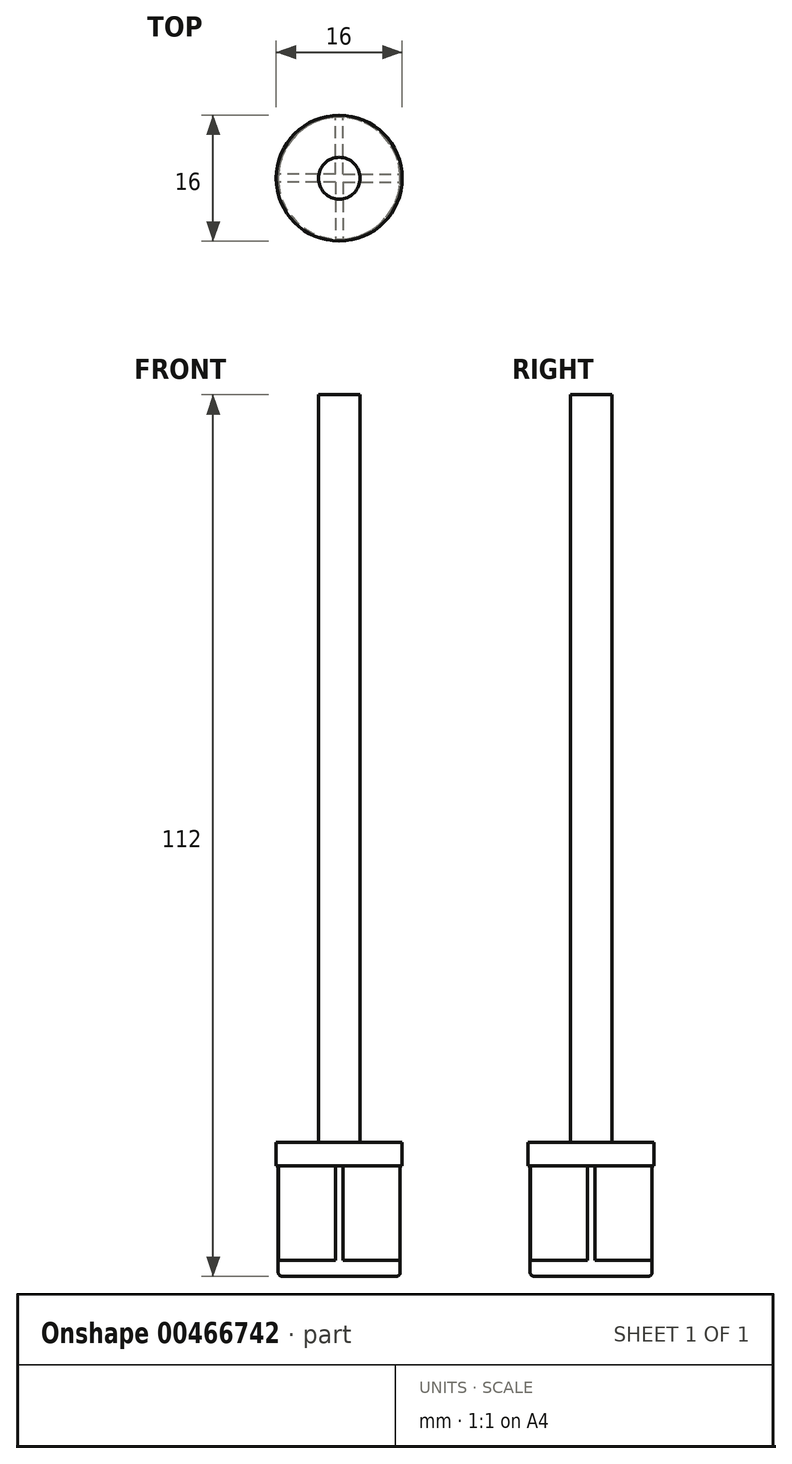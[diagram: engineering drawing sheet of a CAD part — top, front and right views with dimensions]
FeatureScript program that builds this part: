
annotation { "Feature Type Name" : "Feature", "Feature Type Description" : "" }
export const myFeature = defineFeature(function(context is Context, id is Id, definition is map)
    precondition{}
    {
        {
            var Q0;
            Q0=qCreatedBy(makeId("Top.planeOp"),FACE);
            var sketch = newSketch(context, id + "F0", { "sketchPlane" : qUnion([Q0])});
            skCircle(sketch, "E0", {"center": v(0, 0) * mm, "radius": 7.75 * mm});
            skSolve(sketch);
        }
        {
            var Q0;
            Q0=makeQuery(id+"F0.imprint","IMPRINT",FACE,{"disambiguationData":[TD([[makeQuery(id+"F0.imprint","IMPRINT",EDGE,{"derivedFrom":sQuery(id+"F0.wireOp",EDGE,"E0")}),1.0]])]});
            extrude(context, id + "F1", {"entities" : qUnion([Q0]), "depth" : 2 * mm, "offsetDistance" : 25 * mm});
        }
        {
            var Q0;
            Q0=makeQuery(id+"F1.opExtrude","CAP_FACE",FACE,{"disambiguationData":[OSD([sQuery(id+"F0.wireOp",EDGE,"E0")])],"isStart":false});
            var sketch = newSketch(context, id + "F2", { "sketchPlane" : qUnion([Q0])});
            skPoint(sketch, "E1", {"position": v(0, 3.88) * mm});
            skPoint(sketch, "E2", {"position": v(-3.88, 0) * mm});
            skPoint(sketch, "E3", {"position": v(0, -3.88) * mm});
            skPoint(sketch, "E4", {"position": v(3.88, 0) * mm});
            skLineSegment(sketch, "E5.top", {"start": v(0.5, 7.75) * mm, "end": v(-0.5, 7.75) * mm});
            skLineSegment(sketch, "E5.left", {"start": v(0.5, 0) * mm, "end": v(0.5, 7.75) * mm});
            skLineSegment(sketch, "E5.right", {"start": v(-0.5, 0) * mm, "end": v(-0.5, 7.75) * mm});
            skLineSegment(sketch, "E6.bottom", {"start": v(0, -0.5) * mm, "end": v(-7.75, -0.5) * mm});
            skLineSegment(sketch, "E6.top", {"start": v(0, 0.5) * mm, "end": v(-7.75, 0.5) * mm});
            skLineSegment(sketch, "E6.right", {"start": v(-7.75, -0.5) * mm, "end": v(-7.75, 0.5) * mm});
            skLineSegment(sketch, "E7.bottom", {"start": v(0, 0.5) * mm, "end": v(7.75, 0.5) * mm});
            skLineSegment(sketch, "E7.top", {"start": v(0, -0.5) * mm, "end": v(7.75, -0.5) * mm});
            skLineSegment(sketch, "E7.right", {"start": v(7.75, 0.5) * mm, "end": v(7.75, -0.5) * mm});
            skLineSegment(sketch, "E8.top", {"start": v(0.5, -7.75) * mm, "end": v(-0.5, -7.75) * mm});
            skLineSegment(sketch, "E8.left", {"start": v(0.5, 0) * mm, "end": v(0.5, -7.75) * mm});
            skLineSegment(sketch, "E8.right", {"start": v(-0.5, 0) * mm, "end": v(-0.5, -7.75) * mm});
            skSolve(sketch);
        }
        {
            var Q0;
            {var subQ10=sQuery(id+"F2.wireOp",EDGE,"E8.left");var subQ13=sQuery(id+"F2.wireOp",EDGE,"E5.left");var subQ15=makeQuery(id+"F2.imprint","INTERSECT",VERTEX,{"derivedFrom":[subQ13,subQ10]});Q0=makeQuery(id+"F2.imprint","IMPRINT",FACE,{"disambiguationData":[TD([[makeQuery(id+"F2.imprint","IMPRINT",EDGE,{"disambiguationData":[TD([[subQ15,-1.0]])],"derivedFrom":subQ13}),1.0]])]});}
            var Q1;
            {var subQ1=sQuery(id+"F2.wireOp",EDGE,"E5.right");var subQ5=sQuery(id+"F2.wireOp",EDGE,"E8.right");var subQ6=makeQuery(id+"F2.imprint","INTERSECT",VERTEX,{"derivedFrom":[subQ1,subQ5]});Q1=makeQuery(id+"F2.imprint","IMPRINT",FACE,{"disambiguationData":[TD([[makeQuery(id+"F2.imprint","IMPRINT",EDGE,{"disambiguationData":[TD([[subQ6,-1.0]])],"derivedFrom":subQ1}),1.0]])]});}
            var Q2;
            {var subQ0=sQuery(id+"F2.wireOp",EDGE,"E7.bottom");var subQ3=sQuery(id+"F2.wireOp",EDGE,"E5.left");var subQ4=makeQuery(id+"F2.imprint","INTERSECT",VERTEX,{"derivedFrom":[subQ3,subQ0]});Q2=makeQuery(id+"F2.imprint","IMPRINT",FACE,{"disambiguationData":[TD([[makeQuery(id+"F2.imprint","IMPRINT",EDGE,{"disambiguationData":[TD([[subQ4,-1.0]])],"derivedFrom":subQ3}),1.0]])]});}
            var Q3;
            {var subQ0=sQuery(id+"F2.wireOp",EDGE,"E8.left");var subQ1=sQuery(id+"F2.wireOp",EDGE,"E5.left");var subQ2=makeQuery(id+"F2.imprint","INTERSECT",VERTEX,{"derivedFrom":[subQ1,subQ0]});Q3=makeQuery(id+"F2.imprint","IMPRINT",FACE,{"disambiguationData":[TD([[makeQuery(id+"F2.imprint","IMPRINT",EDGE,{"disambiguationData":[TD([[subQ2,-1.0]])],"derivedFrom":subQ1}),-1.0]])]});}
            var Q4;
            {var subQ1=sQuery(id+"F2.wireOp",EDGE,"E6.bottom");var subQ5=sQuery(id+"F2.wireOp",EDGE,"E7.top");var subQ6=makeQuery(id+"F2.imprint","INTERSECT",VERTEX,{"derivedFrom":[subQ1,subQ5]});Q4=makeQuery(id+"F2.imprint","IMPRINT",FACE,{"disambiguationData":[TD([[makeQuery(id+"F2.imprint","IMPRINT",EDGE,{"disambiguationData":[TD([[subQ6,-1.0]])],"derivedFrom":subQ1}),1.0]])]});}
            extrude(context, id + "F3", {"entities" : qUnion([Q0, Q1, Q2, Q3, Q4]), "operationType" : NewBodyOperationType.ADD, "depth" : 12 * mm, "offsetDistance" : 25 * mm});
        }
        {
            var Q0;
            Q0=makeQuery(id+"F3.opExtrude","CAP_FACE",FACE,{"disambiguationData":[OSD([sQuery(id+"F0.wireOp",EDGE,"E0"),sQuery(id+"F2.wireOp",EDGE,"E5.left"),sQuery(id+"F2.wireOp",EDGE,"E5.right"),sQuery(id+"F2.wireOp",EDGE,"E6.bottom"),sQuery(id+"F2.wireOp",EDGE,"E6.top"),sQuery(id+"F2.wireOp",EDGE,"E7.bottom"),sQuery(id+"F2.wireOp",EDGE,"E7.top"),sQuery(id+"F2.wireOp",EDGE,"E8.left"),sQuery(id+"F2.wireOp",EDGE,"E8.right")])],"isStart":false});
            var sketch = newSketch(context, id + "F4", { "sketchPlane" : qUnion([Q0])});
            skCircle(sketch, "E9", {"center": v(0, 0) * mm, "radius": 8 * mm});
            skSolve(sketch);
        }
        {
            var Q0;
            Q0=makeQuery(id+"F4.imprint","IMPRINT",FACE,{"disambiguationData":[TD([[makeQuery(id+"F4.imprint","IMPRINT",EDGE,{"derivedFrom":sQuery(id+"F4.wireOp",EDGE,"E9")}),1.0]])]});
            var Q1;
            {var subQ7=sQuery(id+"F2.wireOp",EDGE,"E5.left");Q1=makeQuery(id+"F4.imprint","IMPRINT",FACE,{"disambiguationData":[TD([[makeQuery(id+"F4.imprint","IMPRINT",EDGE,{"derivedFrom":makeQuery(id+"F3.opExtrude","CAP_EDGE",EDGE,{"disambiguationData":[OSD([subQ7])],"isStart":false})}),1.0]])]});}
            extrude(context, id + "F5", {"entities" : qUnion([Q0, Q1]), "operationType" : NewBodyOperationType.ADD, "depth" : 3 * mm, "offsetDistance" : 25 * mm});
        }
        {
            var Q0;
            Q0=makeQuery(id+"F1.opExtrude","CAP_EDGE",EDGE,{"disambiguationData":[OSD([sQuery(id+"F0.wireOp",EDGE,"E0")])],"isStart":true});
            fillet(context, id + "F6", {"entities" : qUnion([Q0]), "radius" : .5 * mm, "tangentPropagation" : true, "allowEdgeOverflow" : false});
        }
        {
            var Q0;
            Q0=makeQuery(id+"F5.opExtrude","CAP_FACE",FACE,{"disambiguationData":[OSD([sQuery(id+"F4.wireOp",EDGE,"E9")])],"isStart":false});
            var sketch = newSketch(context, id + "F7", { "sketchPlane" : qUnion([Q0])});
            skCircle(sketch, "E10", {"center": v(0, 0) * mm, "radius": 2.65 * mm});
            skSolve(sketch);
        }
        {
            var Q0;
            Q0=makeQuery(id+"F7.imprint","IMPRINT",FACE,{"disambiguationData":[TD([[makeQuery(id+"F7.imprint","IMPRINT",EDGE,{"derivedFrom":sQuery(id+"F7.wireOp",EDGE,"E10")}),1.0]])]});
            extrude(context, id + "F8", {"entities" : qUnion([Q0]), "operationType" : NewBodyOperationType.ADD, "depth" : 95 * mm, "offsetDistance" : 25 * mm});
        }
    });
